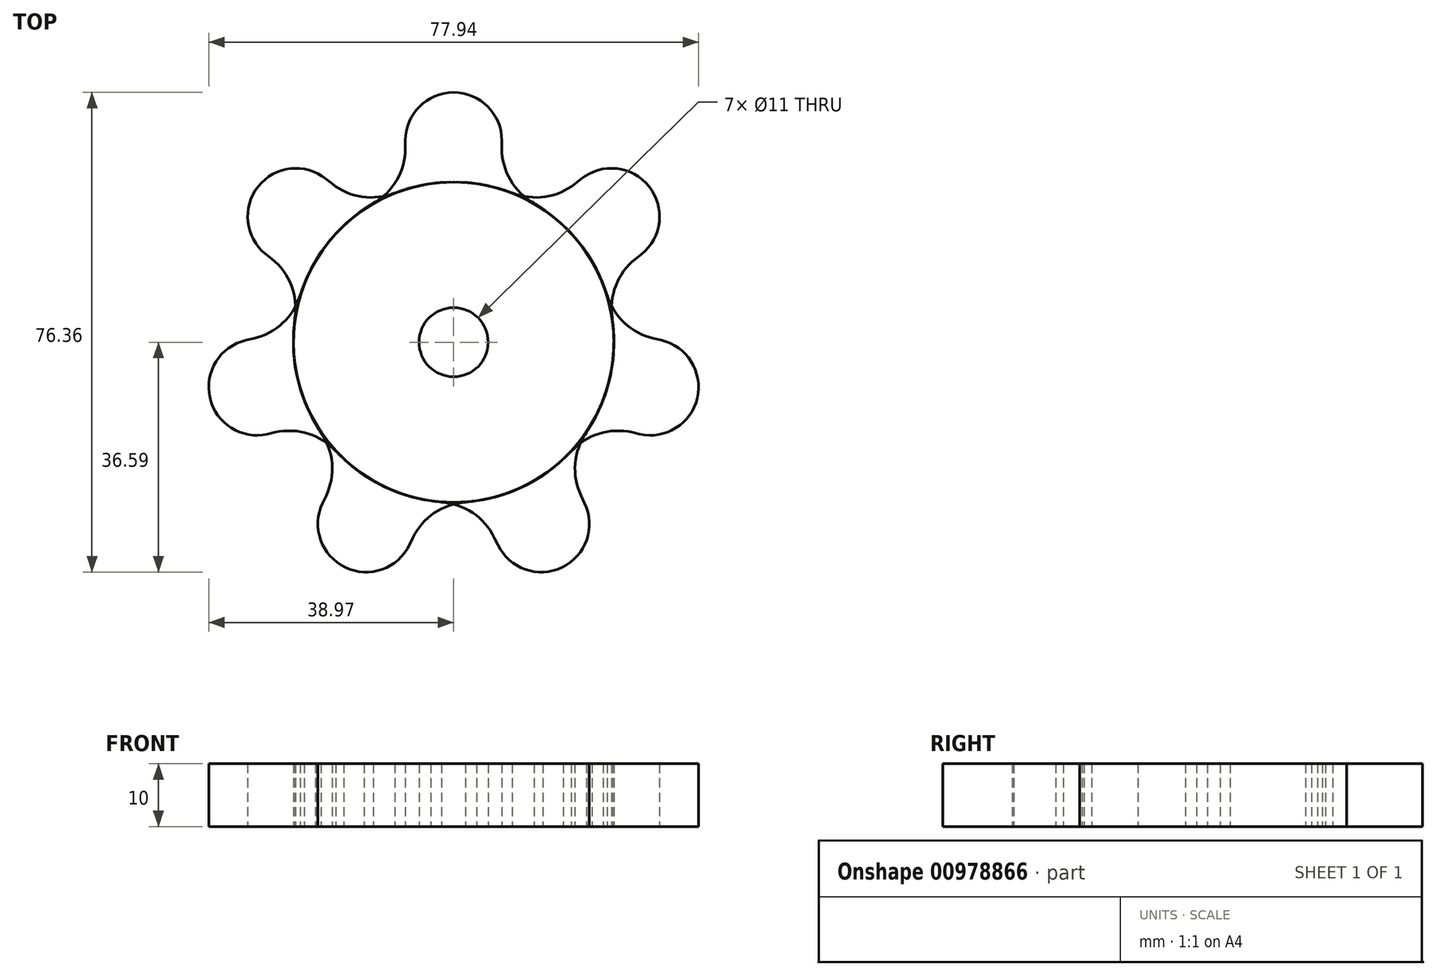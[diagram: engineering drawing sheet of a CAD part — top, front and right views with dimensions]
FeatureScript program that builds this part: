
annotation { "Feature Type Name" : "Feature", "Feature Type Description" : "" }
export const myFeature = defineFeature(function(context is Context, id is Id, definition is map)
    precondition{}
    {
        {
            var Q0;
            Q0=qCreatedBy(makeId("Top.planeOp"),FACE);
            var sketch = newSketch(context, id + "F0", { "sketchPlane" : qUnion([Q0])});
            skCircle(sketch, "E0", {"center": v(0, 0) * mm, "radius": 5.5 * mm});
            skCircle(sketch, "E1.0", {"center": v(0, 0) * mm, "radius": 25.5 * mm});
            skSolve(sketch);
        }
        {
            var Q0;
            Q0 = qSketchRegion(id + "F0", true);
            extrude(context, id + "F1", {"entities" : qUnion([Q0]), "depth" : 10 * mm, "offsetDistance" : 25 * mm});
        }
        {
            var Q0;
            Q0=qCreatedBy(makeId("Top.planeOp"),FACE);
            var sketch = newSketch(context, id + "F2", { "sketchPlane" : qUnion([Q0])});
            skArc(sketch, "E2.0", {"start": v(7.67, 24.32) * mm, "mid": v(0, 25.5) * mm, "end": v(-7.67, 24.32) * mm});
            skLineSegment(sketch, "E3", {"start": v(0, 25.5) * mm, "end": v(0, 32.1) * mm, "construction": true});
            skArc(sketch, "E4.0.endCap", {"start": v(-7.67, 32.1) * mm, "mid": v(0, 39.77) * mm, "end": v(7.67, 32.1) * mm});
            skLineSegment(sketch, "E4.0.left", {"start": v(-7.67, 30.86) * mm, "end": v(-7.67, 32.1) * mm});
            skLineSegment(sketch, "E4.0.right", {"start": v(7.67, 30.86) * mm, "end": v(7.67, 32.1) * mm});
            skArc(sketch, "E5", {"start": v(12.67, 22.2) * mm, "mid": v(-0.06, 25.47) * mm, "end": v(-12.78, 22.13) * mm});
            skArc(sketch, "E6", {"start": v(12.78, 22.13) * mm, "mid": v(0.06, 25.47) * mm, "end": v(-12.67, 22.2) * mm});
            skArc(sketch, "E7", {"start": v(7.67, 24.32) * mm, "mid": v(0, 25.47) * mm, "end": v(-7.67, 24.32) * mm});
            skPoint(sketch, "E8.visualSharp", {"position": v(-7.67, 24.32) * mm});
            skArc(sketch, "E8.filletArc", {"start": v(-12.78, 22.13) * mm, "mid": v(-9.04, 25.8) * mm, "end": v(-7.67, 30.86) * mm});
            skPoint(sketch, "E9.visualSharp", {"position": v(7.67, 24.32) * mm});
            skArc(sketch, "E9.filletArc", {"start": v(7.67, 30.86) * mm, "mid": v(9.04, 25.8) * mm, "end": v(12.78, 22.13) * mm});
            skSolve(sketch);
        }
        {
            var Q0;
            Q0 = qSketchRegion(id + "F2", true);
            var Q1;
            Q1=makeQuery(id+"F1.opExtrude","CAP_FACE",FACE,{"disambiguationData":[OSD([sQuery(id+"F0.wireOp",EDGE,"E0"),sQuery(id+"F0.wireOp",EDGE,"E1.0")])],"isStart":false});
            extrude(context, id + "F3", {"entities" : qUnion([Q0]), "operationType" : NewBodyOperationType.ADD, "endBound" : BoundingType.UP_TO_SURFACE, "depth" : 25 * mm, "endBoundEntityFace" : qUnion([Q1]), "offsetDistance" : 25 * mm});
        }
        {
            var Q0;
            Q0=makeQuery(id+"F1.opExtrude","SWEPT_BODY",BODY,{"disambiguationData":[OSD([sQuery(id+"F0.wireOp",EDGE,"E0"),sQuery(id+"F0.wireOp",EDGE,"E1.0")])]});
            var Q1;
            Q1=makeQuery(id+"F1.opExtrude","SWEPT_FACE",FACE,{"disambiguationData":[OSD([sQuery(id+"F0.wireOp",EDGE,"E0")])]});
            circularPattern(context, id + "F4", {"entities" : qUnion([Q0]), "axis" : qUnion([Q1]), "angle" : 360 * degree, "instanceCount" : 7, "equalSpace" : true});
        }
    });
